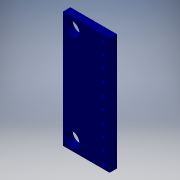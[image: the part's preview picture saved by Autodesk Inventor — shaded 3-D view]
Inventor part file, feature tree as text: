
AUTODESK INVENTOR PART (.ipt)
format: ipt  version: 2018 (Build 220112000, 112)  size: 137,216 bytes
history: native  units: mm
features: extrude x1, sketch x1
ambient origin geometry x8: Origin, YZ Plane, XZ Plane, XY Plane, X Axis, Y Axis, Z Axis, Center Point
bodies: Body1 (feature_tree)
feature tree (2):
  extrude  "Extrusion2"  Depth=25.0mm
  sketch  "Sketch1"  dims[d0=15.0mm d1=25.0mm d2=3.0mm d3=2.25mm d4=3.0mm d5=20.5mm d6=2.25mm d7=2.0mm d8=2.0mm d11=1.5mm d12=1.0mm d13=1.07mm d14=100.0mm d16=2.54mm d17=10.0mm d19=10.0mm d21=1.07mm d22=1.57mm d23=0.0mm]
